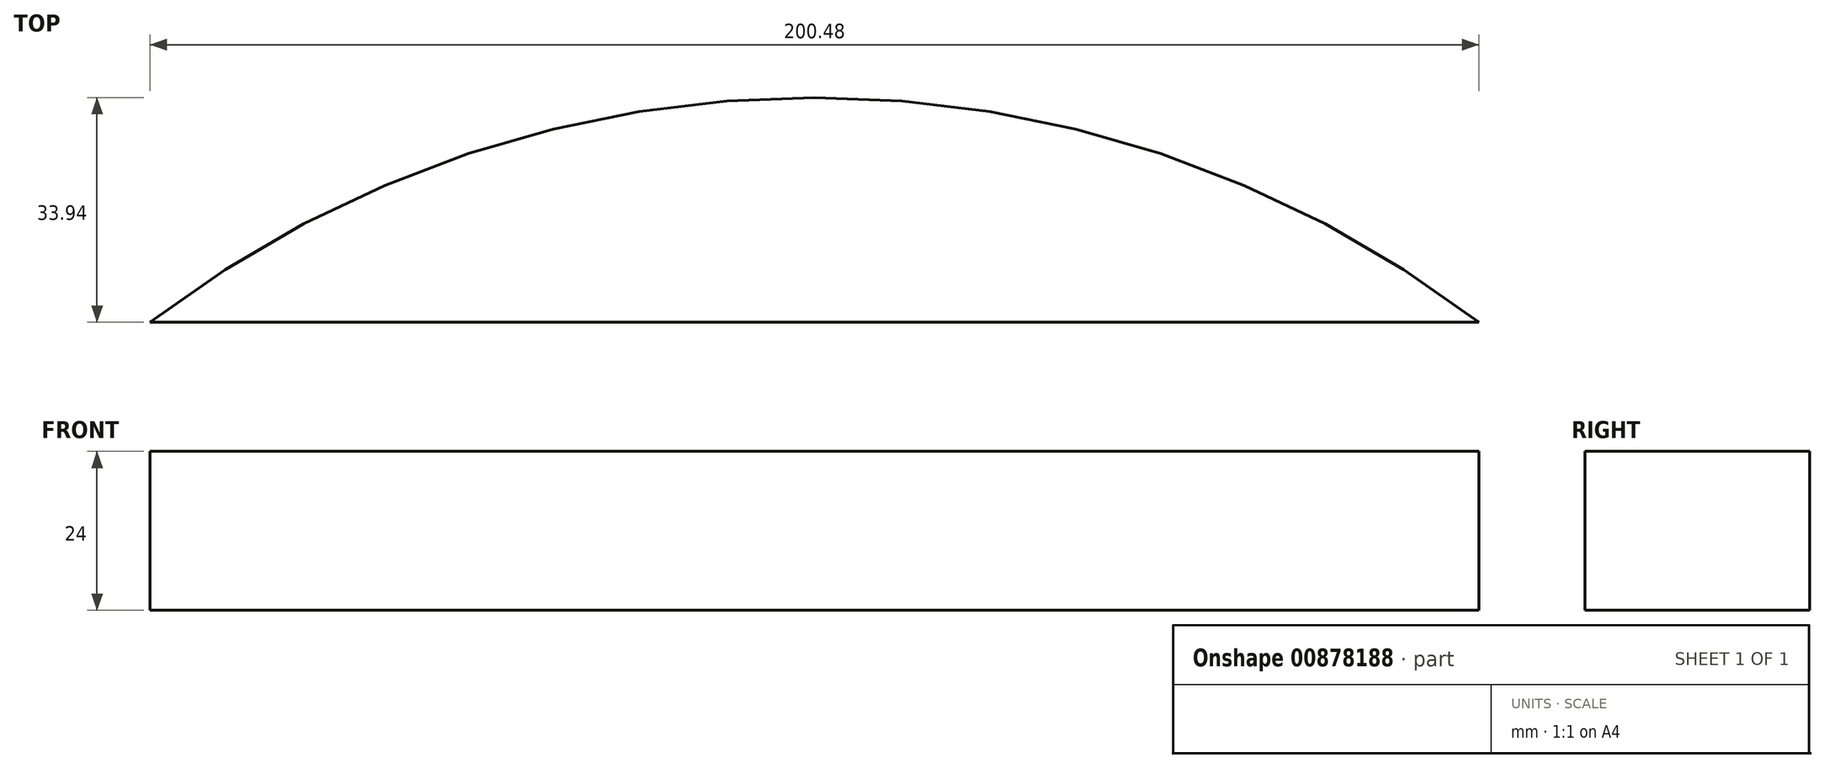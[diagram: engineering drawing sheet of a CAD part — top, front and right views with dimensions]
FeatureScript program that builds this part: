
annotation { "Feature Type Name" : "Feature", "Feature Type Description" : "" }
export const myFeature = defineFeature(function(context is Context, id is Id, definition is map)
    precondition{}
    {
        {
            var Q0;
            Q0=qCreatedBy(makeId("Top.planeOp"),FACE);
            var sketch = newSketch(context, id + "F0", { "sketchPlane" : qUnion([Q0])});
            skCircle(sketch, "E0", {"center": v(0, 0) * mm, "radius": 165 * mm});
            skLineSegment(sketch, "E1", {"start": v(-100.24, 131.06) * mm, "end": v(100.24, 131.06) * mm});
            skSolve(sketch);
        }
        {
            var Q0;
            {var subQ0=sQuery(id+"F0.wireOp",EDGE,"E1");Q0=makeQuery(id+"F0.imprint","IMPRINT",FACE,{"disambiguationData":[TD([[makeQuery(id+"F0.imprint","IMPRINT",EDGE,{"derivedFrom":subQ0}),1.0]])]});}
            extrude(context, id + "F1", {"entities" : qUnion([Q0]), "depth" : 24 * mm, "offsetDistance" : 25 * mm});
        }
    });
